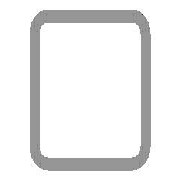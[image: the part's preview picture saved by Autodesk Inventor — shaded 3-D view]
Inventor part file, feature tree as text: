
AUTODESK INVENTOR PART (.ipt)
format: ipt  version: 2025 (Build 290162010, 162A)  size: 132,608 bytes
history: native  units: mm (DEFAULTED — no unit token found)
features: other x4, sketch x1, plane x1
ambient origin geometry x8: Origin, YZ Plane, XZ Plane, XY Plane, X Axis, Y Axis, Z Axis, Center Point
bodies: Solid1 (feature_tree), Body (feature_tree)
feature tree (6):
  parser-record x1  (decoder bookkeeping rows leaked as tree rows — omitted from the tree; the rows remain in map.json)
  other  "Driven Length"
  other  "Start Plane"
  other  "End Plane"
  sketch  "Sketch3"  dims[d3=950.0mm d4=0.0mm d7=8.0mm d9=50.0mm d11=50.0mm d12=4.0mm d13=-0.0mm d14=950.0mm d15=25.0mm d16=25.0mm d17=90.0deg d18=950.0mm]
  plane  "Work Plane3"
